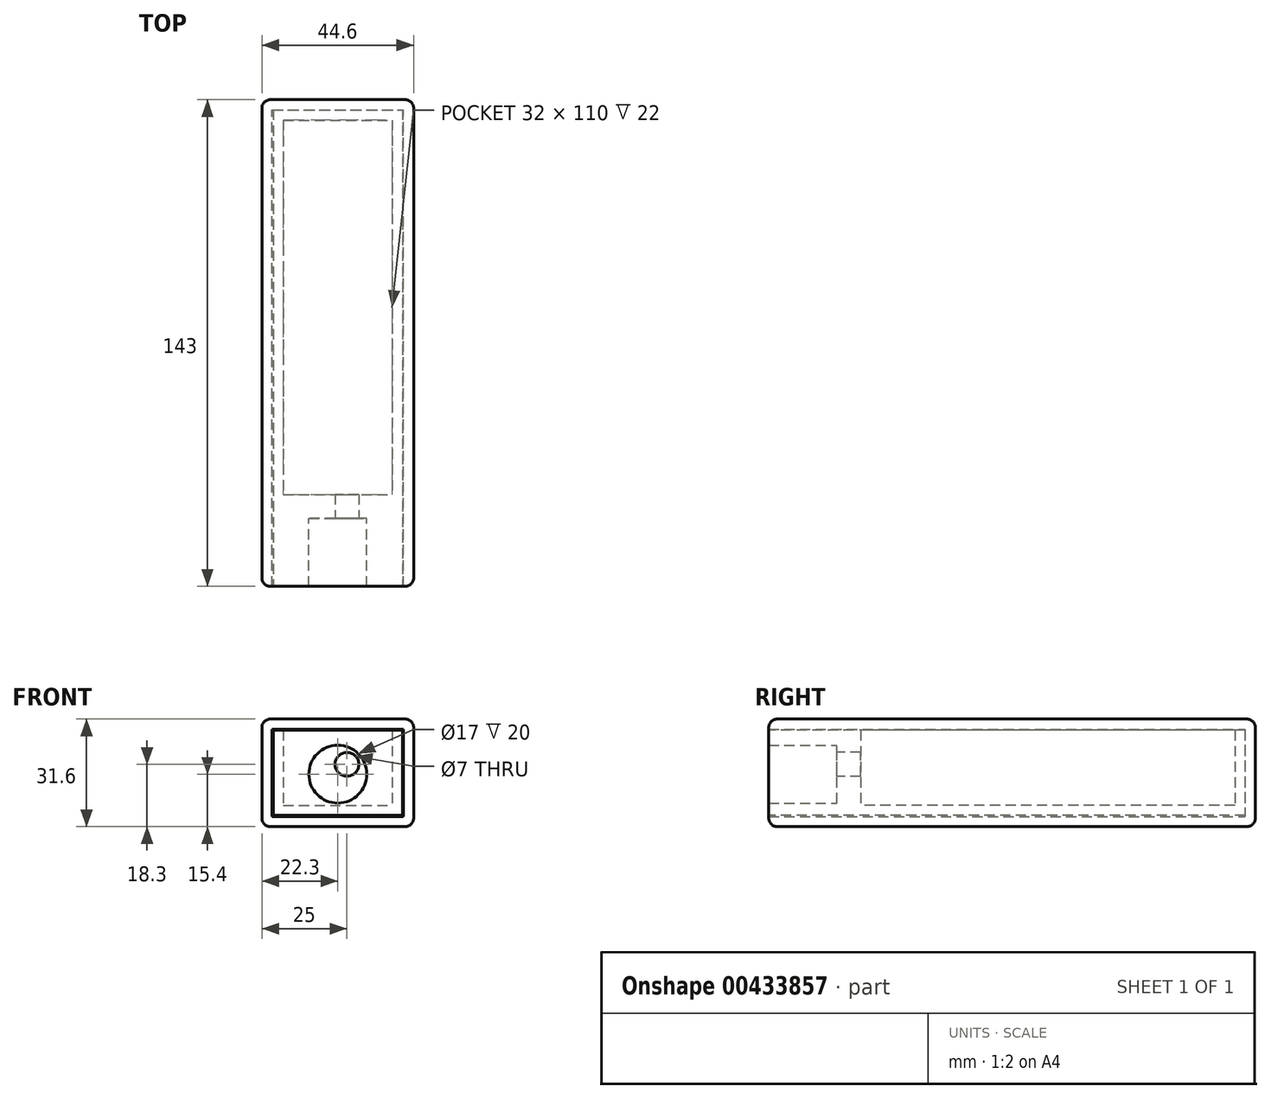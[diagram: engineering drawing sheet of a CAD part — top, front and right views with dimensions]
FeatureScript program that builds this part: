
annotation { "Feature Type Name" : "Feature", "Feature Type Description" : "" }
export const myFeature = defineFeature(function(context is Context, id is Id, definition is map)
    precondition{}
    {
        {
            var Q0;
            Q0=qCreatedBy(makeId("Top.planeOp"),FACE);
            var sketch = newSketch(context, id + "F0", { "sketchPlane" : qUnion([Q0])});
            skLineSegment(sketch, "E0", {"start": v(0, 110) * mm, "end": v(-16, 110) * mm});
            skLineSegment(sketch, "E1", {"start": v(-16, 110) * mm, "end": v(-16, 50) * mm});
            skLineSegment(sketch, "E2", {"start": v(-16, 50) * mm, "end": v(-16, 50) * mm});
            skLineSegment(sketch, "E3", {"start": v(-16, 50) * mm, "end": v(-16, 0) * mm});
            skLineSegment(sketch, "E4", {"start": v(-16, 0) * mm, "end": v(0, 0) * mm});
            skLineSegment(sketch, "E5", {"start": v(0, -88.81) * mm, "end": v(0, 168.2) * mm, "construction": true});
            skLineSegment(sketch, "E6.MirrorCS", {"start": v(0, 110) * mm, "end": v(16, 110) * mm});
            skLineSegment(sketch, "E7.MirrorCS", {"start": v(16, 110) * mm, "end": v(16, 50) * mm});
            skLineSegment(sketch, "E8.MirrorCS", {"start": v(16, 50) * mm, "end": v(16, 50) * mm});
            skLineSegment(sketch, "E9.MirrorCS", {"start": v(16, 50) * mm, "end": v(16, 0) * mm});
            skLineSegment(sketch, "E10.MirrorCS", {"start": v(16, 0) * mm, "end": v(0, 0) * mm});
            skLineSegment(sketch, "E11.0", {"start": v(0, 113) * mm, "end": v(-19, 113) * mm});
            skLineSegment(sketch, "E11.1", {"start": v(0, 113) * mm, "end": v(19, 113) * mm});
            skLineSegment(sketch, "E11.2", {"start": v(-19, 113) * mm, "end": v(-19, 47) * mm});
            skLineSegment(sketch, "E11.3", {"start": v(19, 113) * mm, "end": v(19, 47) * mm});
            skLineSegment(sketch, "E11.4", {"start": v(19, 47) * mm, "end": v(19, 47) * mm});
            skLineSegment(sketch, "E11.5", {"start": v(19, 47) * mm, "end": v(19, -3) * mm});
            skLineSegment(sketch, "E11.6", {"start": v(-19, 47) * mm, "end": v(-19, 47) * mm});
            skLineSegment(sketch, "E11.7", {"start": v(-19, 47) * mm, "end": v(-19, -3) * mm});
            skLineSegment(sketch, "E12", {"start": v(-19, -3) * mm, "end": v(-19, -7) * mm});
            skLineSegment(sketch, "E13", {"start": v(-19, -7) * mm, "end": v(0, -7) * mm});
            skLineSegment(sketch, "E14.MirrorCS", {"start": v(19, -7) * mm, "end": v(0, -7) * mm});
            skLineSegment(sketch, "E15.MirrorCS", {"start": v(19, -3) * mm, "end": v(19, -7) * mm});
            skSolve(sketch);
        }
        {
            var Q0;
            Q0=makeQuery(id+"F0.imprint","IMPRINT",FACE,{"disambiguationData":[TD([[makeQuery(id+"F0.imprint","IMPRINT",EDGE,{"derivedFrom":sQuery(id+"F0.wireOp",EDGE,"E0")}),1.0]])]});
            extrude(context, id + "F1", {"entities" : qUnion([Q0]), "depth" : 3 * mm});
        }
        {
            var Q0;
            Q0=makeQuery(id+"F0.imprint","IMPRINT",FACE,{"disambiguationData":[TD([[makeQuery(id+"F0.imprint","IMPRINT",EDGE,{"derivedFrom":sQuery(id+"F0.wireOp",EDGE,"E0")}),-1.0]])]});
            extrude(context, id + "F2", {"entities" : qUnion([Q0]), "operationType" : NewBodyOperationType.ADD, "depth" : 25 * mm});
        }
        {
            var Q0;
            Q0=makeQuery(id+"F2.opExtrude","SWEPT_FACE",FACE,{"disambiguationData":[OSD([sQuery(id+"F0.wireOp",EDGE,"E11.0"),sQuery(id+"F0.wireOp",EDGE,"E11.1")])]});
            var sketch = newSketch(context, id + "F3", { "sketchPlane" : qUnion([Q0])});
            skLineSegment(sketch, "E16.0", {"start": v(19.3, 25.3) * mm, "end": v(-19.3, 25.3) * mm});
            skLineSegment(sketch, "E16.1", {"start": v(19.3, 25.3) * mm, "end": v(19.3, -0.3) * mm});
            skLineSegment(sketch, "E16.2", {"start": v(19.3, -0.3) * mm, "end": v(-19.3, -0.3) * mm});
            skLineSegment(sketch, "E16.3", {"start": v(-19.3, 25.3) * mm, "end": v(-19.3, -0.3) * mm});
            skLineSegment(sketch, "E17.0", {"start": v(22.3, 28.3) * mm, "end": v(-22.3, 28.3) * mm});
            skLineSegment(sketch, "E17.1", {"start": v(22.3, 28.3) * mm, "end": v(22.3, -3.3) * mm});
            skLineSegment(sketch, "E17.2", {"start": v(22.3, -3.3) * mm, "end": v(-22.3, -3.3) * mm});
            skLineSegment(sketch, "E17.3", {"start": v(-22.3, 28.3) * mm, "end": v(-22.3, -3.3) * mm});
            skSolve(sketch);
        }
        {
            var Q0;
            Q0=makeQuery(id+"F3.imprint","IMPRINT",FACE,{"disambiguationData":[TD([[makeQuery(id+"F3.imprint","IMPRINT",EDGE,{"derivedFrom":sQuery(id+"F3.wireOp",EDGE,"E16.0")}),-1.0]])]});
            extrude(context, id + "F4", {"entities" : qUnion([Q0]), "oppositeDirection" : true, "depth" : 140 * mm});
        }
        {
            var Q0;
            Q0=makeQuery(id+"F3.imprint","IMPRINT",FACE,{"disambiguationData":[TD([[makeQuery(id+"F3.imprint","IMPRINT",EDGE,{"derivedFrom":sQuery(id+"F3.wireOp",EDGE,"E16.0")}),-1.0]])]});
            var Q1;
            Q1=makeQuery(id+"F3.imprint","IMPRINT",FACE,{"disambiguationData":[TD([[makeQuery(id+"F3.imprint","IMPRINT",EDGE,{"derivedFrom":sQuery(id+"F3.wireOp",EDGE,"E16.0")}),1.0]])]});
            var Q2;
            {var subQ0=sQuery(id+"F0.wireOp",EDGE,"E11.0");Q2=makeQuery(id+"F3.imprint","IMPRINT",FACE,{"disambiguationData":[TD([[makeQuery(id+"F3.imprint","IMPRINT",EDGE,{"derivedFrom":makeQuery(id+"F2.opExtrude","SWEPT_EDGE",EDGE,{"disambiguationData":[OSD([subQ0,sQuery(id+"F0.wireOp",EDGE,"E11.2")])]})}),-1.0]])]});}
            extrude(context, id + "F5", {"entities" : qUnion([Q0, Q1, Q2]), "operationType" : NewBodyOperationType.ADD, "depth" : 3 * mm});
        }
        {
            var Q0;
            Q0=makeQuery(id+"F2.opExtrude","SWEPT_FACE",FACE,{"disambiguationData":[OSD([sQuery(id+"F0.wireOp",EDGE,"E13"),sQuery(id+"F0.wireOp",EDGE,"E14.MirrorCS")])]});
            var sketch = newSketch(context, id + "F6", { "sketchPlane" : qUnion([Q0])});
            skCircle(sketch, "E18", {"center": v(0, 12.1) * mm, "radius": 8.5 * mm});
            skCircle(sketch, "E19", {"center": v(2.7, 15) * mm, "radius": 3.5 * mm});
            skSolve(sketch);
        }
        {
            var Q0;
            Q0=makeQuery(id+"F6.imprint","IMPRINT",FACE,{"disambiguationData":[TD([[makeQuery(id+"F6.imprint","IMPRINT",EDGE,{"derivedFrom":sQuery(id+"F6.wireOp",EDGE,"E18")}),-1.0]])]});
            extrude(context, id + "F7", {"entities" : qUnion([Q0]), "operationType" : NewBodyOperationType.ADD, "depth" : 20 * mm});
        }
        {
            var Q0;
            Q0=makeQuery(id+"F6.imprint","IMPRINT",FACE,{"disambiguationData":[TD([[makeQuery(id+"F6.imprint","IMPRINT",EDGE,{"derivedFrom":sQuery(id+"F6.wireOp",EDGE,"E19")}),1.0]])]});
            extrude(context, id + "F8", {"entities" : qUnion([Q0]), "operationType" : NewBodyOperationType.REMOVE, "endBound" : BoundingType.UP_TO_NEXT, "oppositeDirection" : true, "depth" : 25 * mm});
        }
        {
            var Q0;
            Q0=makeQuery(id+"F5.opExtrude","CAP_EDGE",EDGE,{"disambiguationData":[OSD([sQuery(id+"F3.wireOp",EDGE,"E17.2")])],"isStart":false});
            var Q1;
            Q1=makeQuery(id+"F5.opExtrude","CAP_EDGE",EDGE,{"disambiguationData":[OSD([sQuery(id+"F3.wireOp",EDGE,"E17.1")])],"isStart":false});
            var Q2;
            Q2=makeQuery(id+"F5.opExtrude","CAP_EDGE",EDGE,{"disambiguationData":[OSD([sQuery(id+"F3.wireOp",EDGE,"E17.0")])],"isStart":false});
            var Q3;
            Q3=makeQuery(id+"F5.opExtrude","CAP_EDGE",EDGE,{"disambiguationData":[OSD([sQuery(id+"F3.wireOp",EDGE,"E17.3")])],"isStart":false});
            var Q4;
            {var subQ0=sQuery(id+"F3.wireOp",EDGE,"E17.1");var subQ1=sQuery(id+"F3.wireOp",EDGE,"E17.0");Q4=makeQuery(id+"F5.boolean.opBoolean","MERGE",EDGE,{"derivedFrom":[makeQuery(id+"F4.opExtrude","SWEPT_EDGE",EDGE,{"disambiguationData":[OSD([subQ1,subQ0])]}),makeQuery(id+"F5.opExtrude","SWEPT_EDGE",EDGE,{"disambiguationData":[OSD([subQ1,subQ0])]})]});}
            var Q5;
            {var subQ0=sQuery(id+"F3.wireOp",EDGE,"E17.2");var subQ1=sQuery(id+"F3.wireOp",EDGE,"E17.1");Q5=makeQuery(id+"F5.boolean.opBoolean","MERGE",EDGE,{"derivedFrom":[makeQuery(id+"F4.opExtrude","SWEPT_EDGE",EDGE,{"disambiguationData":[OSD([subQ1,subQ0])]}),makeQuery(id+"F5.opExtrude","SWEPT_EDGE",EDGE,{"disambiguationData":[OSD([subQ1,subQ0])]})]});}
            var Q6;
            {var subQ0=sQuery(id+"F3.wireOp",EDGE,"E17.3");var subQ1=sQuery(id+"F3.wireOp",EDGE,"E17.2");Q6=makeQuery(id+"F5.boolean.opBoolean","MERGE",EDGE,{"derivedFrom":[makeQuery(id+"F4.opExtrude","SWEPT_EDGE",EDGE,{"disambiguationData":[OSD([subQ1,subQ0])]}),makeQuery(id+"F5.opExtrude","SWEPT_EDGE",EDGE,{"disambiguationData":[OSD([subQ1,subQ0])]})]});}
            var Q7;
            {var subQ0=sQuery(id+"F3.wireOp",EDGE,"E17.3");var subQ1=sQuery(id+"F3.wireOp",EDGE,"E17.0");Q7=makeQuery(id+"F5.boolean.opBoolean","MERGE",EDGE,{"derivedFrom":[makeQuery(id+"F4.opExtrude","SWEPT_EDGE",EDGE,{"disambiguationData":[OSD([subQ1,subQ0])]}),makeQuery(id+"F5.opExtrude","SWEPT_EDGE",EDGE,{"disambiguationData":[OSD([subQ1,subQ0])]})]});}
            var Q8;
            Q8=makeQuery(id+"F4.opExtrude","CAP_EDGE",EDGE,{"disambiguationData":[OSD([sQuery(id+"F3.wireOp",EDGE,"E17.2")])],"isStart":false});
            var Q9;
            Q9=makeQuery(id+"F4.opExtrude","CAP_EDGE",EDGE,{"disambiguationData":[OSD([sQuery(id+"F3.wireOp",EDGE,"E17.3")])],"isStart":false});
            var Q10;
            Q10=makeQuery(id+"F4.opExtrude","CAP_EDGE",EDGE,{"disambiguationData":[OSD([sQuery(id+"F3.wireOp",EDGE,"E17.0")])],"isStart":false});
            var Q11;
            Q11=makeQuery(id+"F4.opExtrude","CAP_EDGE",EDGE,{"disambiguationData":[OSD([sQuery(id+"F3.wireOp",EDGE,"E17.1")])],"isStart":false});
            fillet(context, id + "F9", {"entities" : qUnion([Q0, Q1, Q2, Q3, Q4, Q5, Q6, Q7, Q8, Q9, Q10, Q11]), "radius" : 2.5 * mm, "tangentPropagation" : true, "allowEdgeOverflow" : false});
        }
    });
